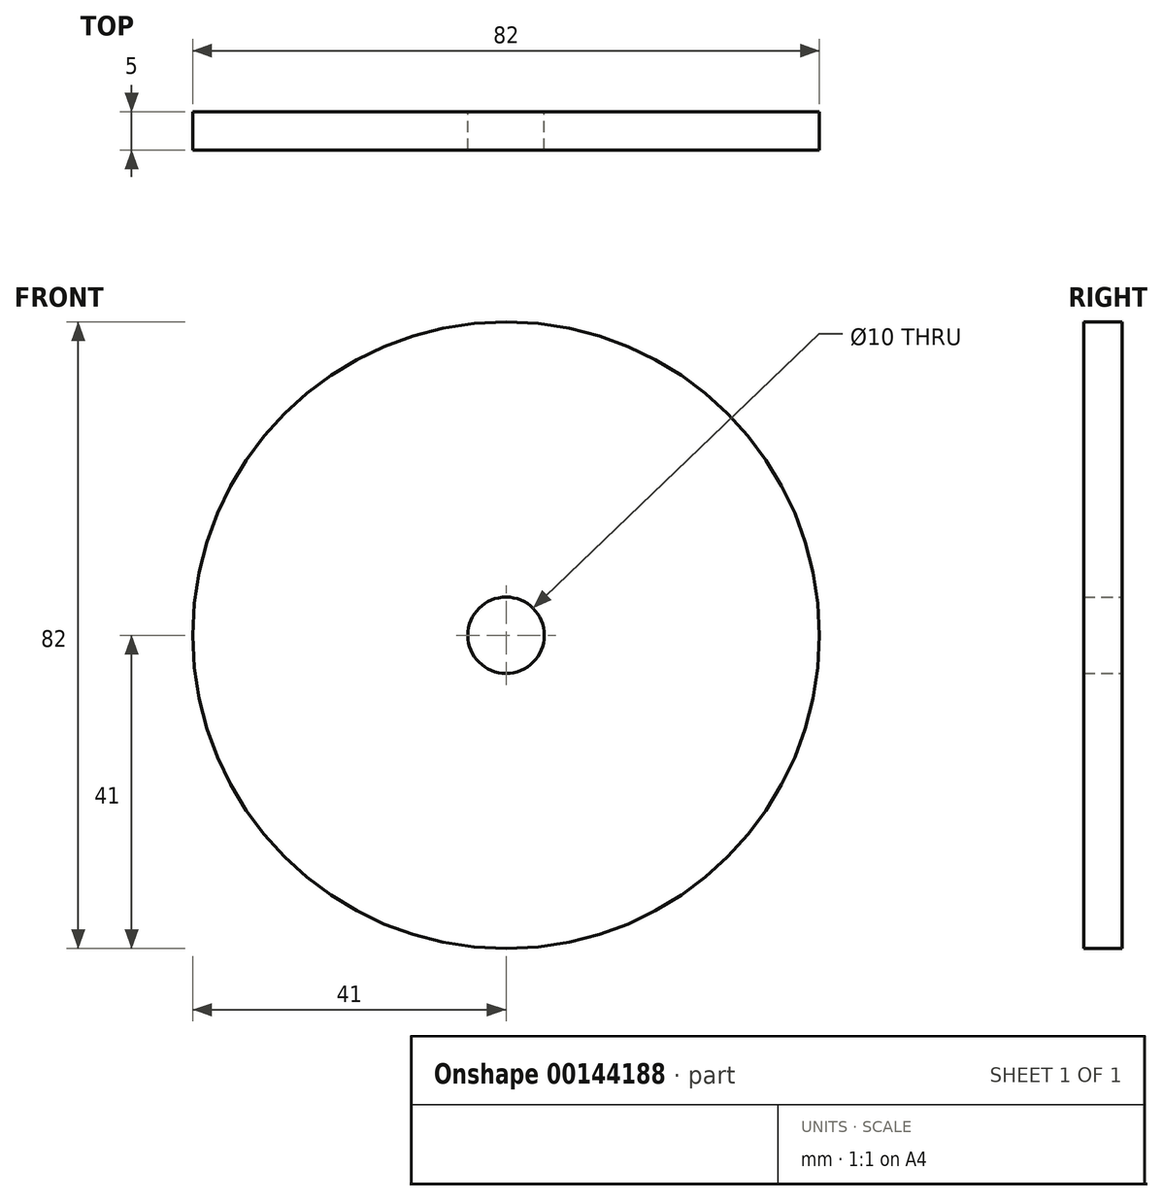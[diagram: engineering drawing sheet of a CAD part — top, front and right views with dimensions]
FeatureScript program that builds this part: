
annotation { "Feature Type Name" : "Feature", "Feature Type Description" : "" }
export const myFeature = defineFeature(function(context is Context, id is Id, definition is map)
    precondition{}
    {
        {
            var Q0;
            Q0=qCreatedBy(makeId("Front.planeOp"),FACE);
            var sketch = newSketch(context, id + "F0", { "sketchPlane" : qUnion([Q0])});
            skCircle(sketch, "E0", {"center": v(0, 0) * mm, "radius": 41 * mm});
            skCircle(sketch, "E1", {"center": v(0, 0) * mm, "radius": 5 * mm});
            skSolve(sketch);
        }
        {
            var Q0;
            Q0 = qSketchRegion(id + "F0", true);
            extrude(context, id + "F1", {"entities" : qUnion([Q0]), "depth" : 5 * mm});
        }
    });
